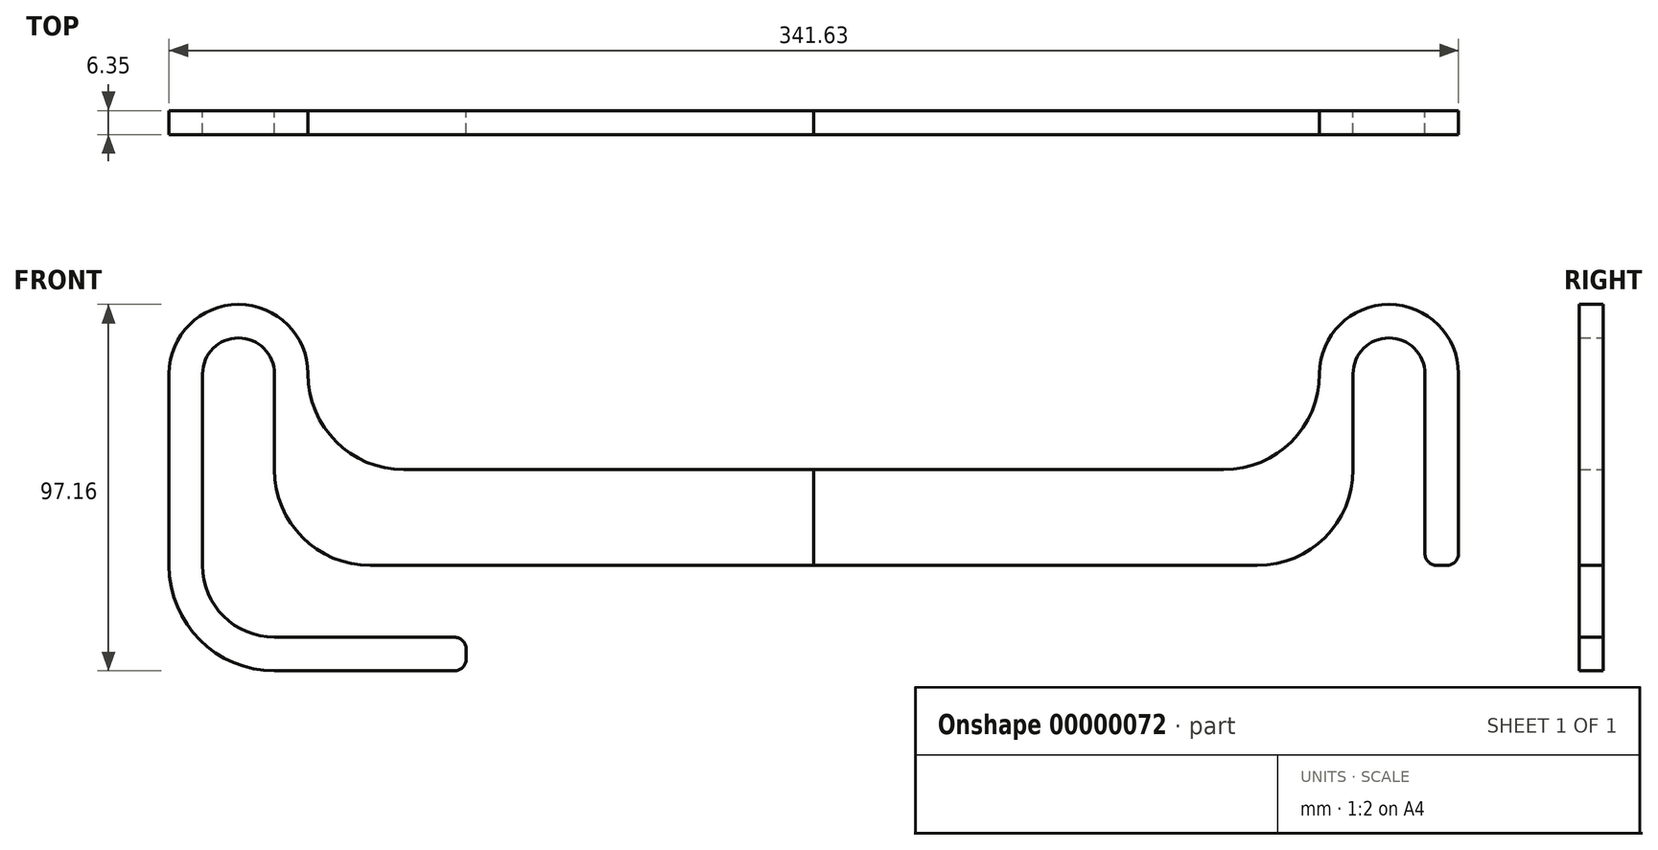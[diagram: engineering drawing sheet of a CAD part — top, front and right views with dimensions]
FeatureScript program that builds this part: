
annotation { "Feature Type Name" : "Feature", "Feature Type Description" : "" }
export const myFeature = defineFeature(function(context is Context, id is Id, definition is map)
    precondition{}
    {
        {
            var Q0;
            Q0=qCreatedBy(makeId("Front.planeOp"),FACE);
            var sketch = newSketch(context, id + "F0", { "sketchPlane" : qUnion([Q0])});
            skLineSegment(sketch, "E0", {"start": v(0, 0) * mm, "end": v(0, 44.88) * mm, "construction": true});
            skLineSegment(sketch, "E1", {"start": v(-108.59, 12.7) * mm, "end": v(0, 12.7) * mm});
            skLineSegment(sketch, "E2", {"start": v(0, 0) * mm, "end": v(-120.65, 0) * mm, "construction": true});
            skLineSegment(sketch, "E3.0.MirrorCS", {"start": v(-117.47, -12.7) * mm, "end": v(0, -12.7) * mm});
            skArc(sketch, "E4.0.MirrorC", {"start": v(-170.81, 38.1) * mm, "mid": v(-152.4, 56.51) * mm, "end": v(-133.99, 38.1) * mm});
            skArc(sketch, "E5.0.MirrorC", {"start": v(-161.93, 38.1) * mm, "mid": v(-152.4, 47.63) * mm, "end": v(-142.88, 38.1) * mm});
            skLineSegment(sketch, "E6", {"start": v(-161.93, 38.1) * mm, "end": v(-161.93, -12.7) * mm});
            skLineSegment(sketch, "E7", {"start": v(-142.88, 38.1) * mm, "end": v(-142.88, 12.7) * mm});
            skLineSegment(sketch, "E8", {"start": v(-170.81, 38.1) * mm, "end": v(-170.81, -12.7) * mm});
            skLineSegment(sketch, "E9", {"start": v(-133.99, 38.1) * mm, "end": v(-133.99, 38.1) * mm});
            skLineSegment(sketch, "E10", {"start": v(-170.81, -12.7) * mm, "end": v(-161.93, -12.7) * mm});
            skPoint(sketch, "E11.visualSharp", {"position": v(-133.99, 12.7) * mm});
            skArc(sketch, "E11.filletArc", {"start": v(-133.99, 38.1) * mm, "mid": v(-126.55, 20.14) * mm, "end": v(-108.59, 12.7) * mm});
            skPoint(sketch, "E12.visualSharp", {"position": v(-142.87, -12.7) * mm});
            skArc(sketch, "E12.filletArc", {"start": v(-142.88, 12.7) * mm, "mid": v(-135.44, -5.26) * mm, "end": v(-117.47, -12.7) * mm});
            skLineSegment(sketch, "E13", {"start": v(0, 12.7) * mm, "end": v(0, -12.7) * mm});
            skArc(sketch, "E14", {"start": v(-170.82, -12.7) * mm, "mid": v(-162.63, -32.46) * mm, "end": v(-142.88, -40.64) * mm});
            skLineSegment(sketch, "E15", {"start": v(-142.88, -40.64) * mm, "end": v(-92.08, -40.64) * mm});
            skLineSegment(sketch, "E16", {"start": v(-92.08, -40.64) * mm, "end": v(-92.08, -31.75) * mm});
            skLineSegment(sketch, "E17", {"start": v(-92.08, -31.75) * mm, "end": v(-142.88, -31.75) * mm});
            skArc(sketch, "E18", {"start": v(-161.93, -12.7) * mm, "mid": v(-156.35, -26.17) * mm, "end": v(-142.88, -31.75) * mm});
            skSolve(sketch);
        }
        {
            var Q0;
            Q0=makeQuery(id+"F0.imprint","IMPRINT",FACE,{"disambiguationData":[TD([[makeQuery(id+"F0.imprint","IMPRINT",EDGE,{"derivedFrom":sQuery(id+"F0.wireOp",EDGE,"E1")}),-1.0]])]});
            extrude(context, id + "F1", {"entities" : qUnion([Q0]), "depth" : 6.35 * mm});
        }
        {
            var Q0;
            Q0=makeQuery(id+"F1.opExtrude","SWEPT_BODY",BODY,{"disambiguationData":[OSD([sQuery(id+"F0.wireOp",EDGE,"E1"),sQuery(id+"F0.wireOp",EDGE,"E3.0.MirrorCS"),sQuery(id+"F0.wireOp",EDGE,"E4.0.MirrorC"),sQuery(id+"F0.wireOp",EDGE,"E5.0.MirrorC"),sQuery(id+"F0.wireOp",EDGE,"E6"),sQuery(id+"F0.wireOp",EDGE,"E7"),sQuery(id+"F0.wireOp",EDGE,"E8"),sQuery(id+"F0.wireOp",EDGE,"E10"),sQuery(id+"F0.wireOp",EDGE,"E11.filletArc"),sQuery(id+"F0.wireOp",EDGE,"E12.filletArc"),sQuery(id+"F0.wireOp",EDGE,"E13")])]});
            var Q1;
            Q1=qCreatedBy(makeId("Right.planeOp"),FACE);
            mirror(context, id + "F2", {"entities" : qUnion([Q0]), "mirrorPlane" : qUnion([Q1])});
        }
        {
            var Q0;
            Q0=makeQuery(id+"F0.imprint","IMPRINT",FACE,{"disambiguationData":[TD([[makeQuery(id+"F0.imprint","IMPRINT",EDGE,{"derivedFrom":sQuery(id+"F0.wireOp",EDGE,"E10")}),-1.0]])]});
            extrude(context, id + "F3", {"entities" : qUnion([Q0]), "operationType" : NewBodyOperationType.ADD, "depth" : 6.35 * mm});
        }
        {
            var Q0;
            Q0=makeQuery(id+"F3.opExtrude","SWEPT_EDGE",EDGE,{"disambiguationData":[OSD([sQuery(id+"F0.wireOp",EDGE,"E16"),sQuery(id+"F0.wireOp",EDGE,"E17")])]});
            var Q1;
            Q1=makeQuery(id+"F3.opExtrude","SWEPT_EDGE",EDGE,{"disambiguationData":[OSD([sQuery(id+"F0.wireOp",EDGE,"E15"),sQuery(id+"F0.wireOp",EDGE,"E16")])]});
            var Q2;
            Q2=makeQuery(id+"F2.opPattern","COPY",EDGE,{"derivedFrom":makeQuery(id+"F1.opExtrude","SWEPT_EDGE",EDGE,{"disambiguationData":[OSD([sQuery(id+"F0.wireOp",EDGE,"E8"),sQuery(id+"F0.wireOp",EDGE,"E10"),sQuery(id+"F0.wireOp",EDGE,"E14")])]}),"instanceName":"1"});
            var Q3;
            Q3=makeQuery(id+"F2.opPattern","COPY",EDGE,{"derivedFrom":makeQuery(id+"F1.opExtrude","SWEPT_EDGE",EDGE,{"disambiguationData":[OSD([sQuery(id+"F0.wireOp",EDGE,"E6"),sQuery(id+"F0.wireOp",EDGE,"E10"),sQuery(id+"F0.wireOp",EDGE,"E18")])]}),"instanceName":"1"});
            fillet(context, id + "F4", {"entities" : qUnion([Q0, Q1, Q2, Q3]), "radius" : 3.17 * mm, "tangentPropagation" : true, "allowEdgeOverflow" : false});
        }
    });
